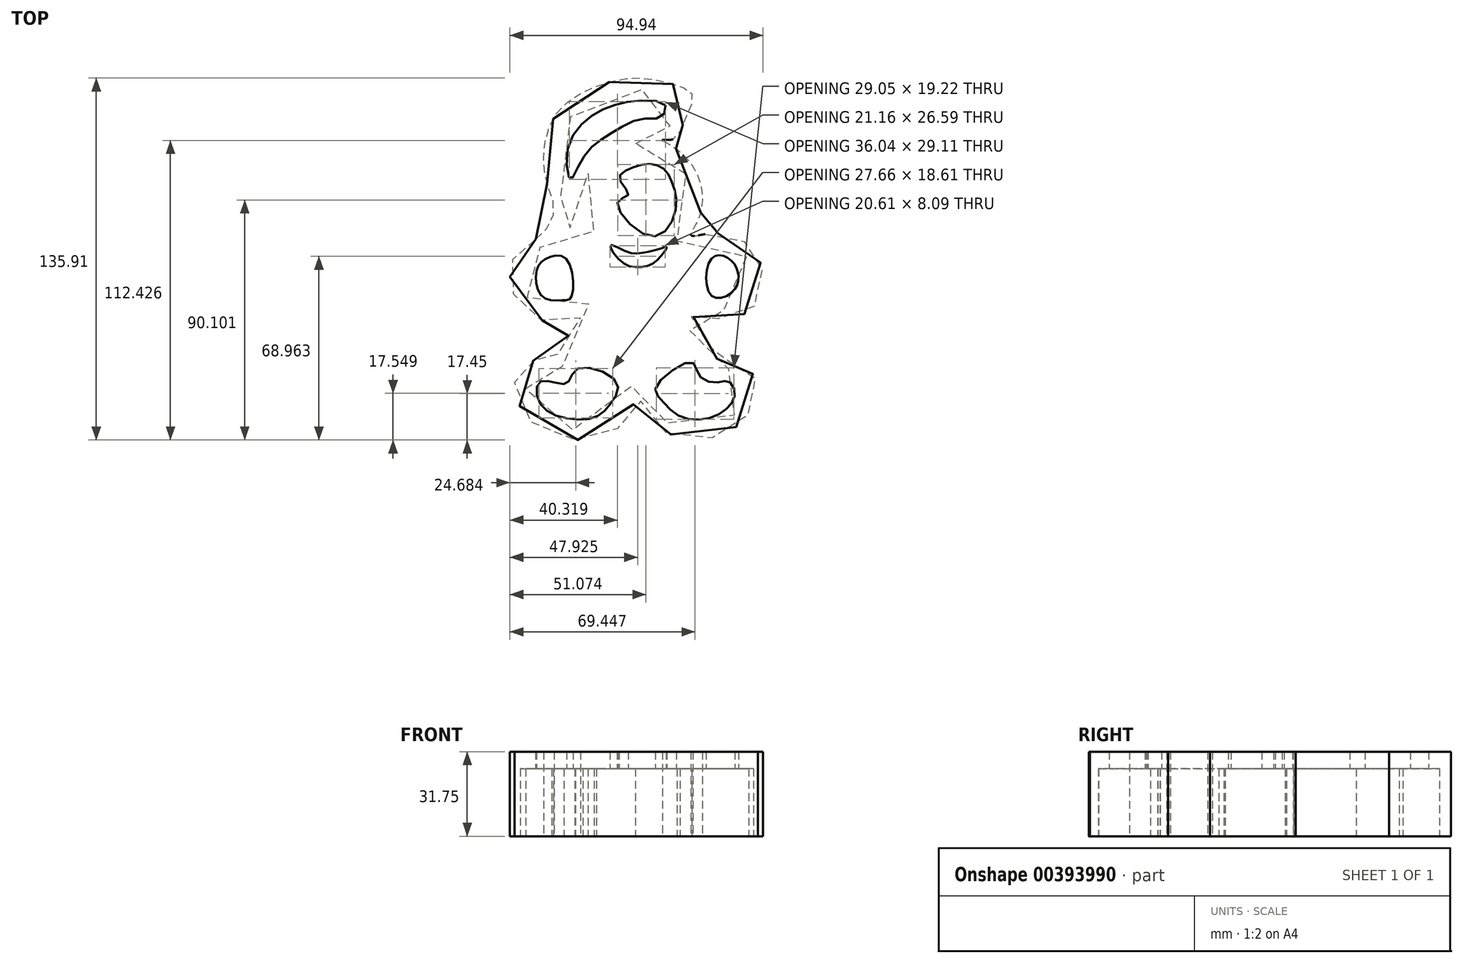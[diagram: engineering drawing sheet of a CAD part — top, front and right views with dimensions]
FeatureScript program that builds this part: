
annotation { "Feature Type Name" : "Feature", "Feature Type Description" : "" }
export const myFeature = defineFeature(function(context is Context, id is Id, definition is map)
    precondition{}
    {
        {
            var Q0;
            Q0=qCreatedBy(makeId("Top.planeOp"),FACE);
            var sketch = newSketch(context, id + "F0", { "sketchPlane" : qUnion([Q0])});
            skFitSpline(sketch, "E0", {"points": [v(2.77, 48.07) * mm, v(4.04, 51.23) * mm, v(6.56, 54.07) * mm, v(12.78, 54.07) * mm, v(14.32, 53.32) * mm, v(19.37, 63.42) * mm, v(15.75, 65.98) * mm, v(7.7, 68.06) * mm, v(-2.72, 67.77) * mm, v(-15.24, 63.3) * mm, v(-24.18, 54.95) * mm, v(-28.06, 42.43) * mm, v(-25.08, 26.94) * mm, v(-24.78, 19.78) * mm, v(-28.65, 13.82) * mm, v(-21.8, 16.5) * mm, v(-20.01, 26.64) * mm, v(-18.82, 33.5) * mm, v(-15.24, 37.07) * mm, v(-16.43, 31.1) * mm, v(-16.73, 23.36) * mm, v(-14.35, 16.8) * mm, v(-11.96, 12.73) * mm, v(-19.66, 10.97) * mm, v(-31.35, 9.54) * mm, v(-36.26, 7.28) * mm, v(-40.24, 0.64) * mm, v(-39.44, -7.19) * mm, v(-36.4, -11.3) * mm, v(-30.95, -14.22) * mm, v(-19.4, -13.3) * mm, v(-13.03, -12.37) * mm, v(-16.21, -20.6) * mm, v(-24.5, -35.1) * mm, v(-26.59, -37.48) * mm, v(-29.57, -36.58) * mm, v(-35.53, -38.07) * mm, v(-38.51, -43.74) * mm, v(-36.42, -50) * mm, v(-30.46, -55.95) * mm, v(-19.74, -59.53) * mm, v(-7.81, -56.85) * mm, v(-0.07, -45.82) * mm, v(2.92, -40.16) * mm, v(6.2, -46.12) * mm, v(12.78, -55.36) * mm, v(21.1, -59.23) * mm, v(32.12, -58.34) * mm, v(40.77, -52.97) * mm, v(44.94, -46.72) * mm, v(43.75, -40.16) * mm, v(37.79, -36.58) * mm, v(32.72, -37.18) * mm, v(28.25, -30.92) * mm, v(24.08, -23.77) * mm, v(19.6, -13.34) * mm, v(26.76, -13.34) * mm, v(36.9, -14.23) * mm, v(45.53, -8.57) * mm, v(46.43, 0.97) * mm, v(42.26, 7.82) * mm, v(30.04, 10.97) * mm, v(18.41, 10.97) * mm, v(20.5, 15.27) * mm, v(23.78, 24.81) * mm, v(21.4, 37.03) * mm, v(16.03, 43.59) * mm, v(10.07, 46.87) * mm, v(2.77, 48.07) * mm]});
            skSolve(sketch);
        }
        {
            var Q0;
            Q0=qCreatedBy(makeId("Top.planeOp"),FACE);
            var sketch = newSketch(context, id + "F1", { "sketchPlane" : qUnion([Q0])});
            skFitSpline(sketch, "E1", {"points": [v(-34.62, 12.22) * mm, v(-27.93, 22.11) * mm, v(-30.26, 32.3) * mm, v(-31.71, 45.1) * mm, v(-27.93, 57.9) * mm, v(-18.33, 66.63) * mm, v(-4.36, 71.86) * mm, v(7.28, 72.45) * mm, v(19.5, 69.54) * mm, v(24.15, 66.05) * mm, v(20.95, 56.44) * mm, v(16.88, 49.75) * mm, v(12.8, 49.46) * mm, v(17.75, 46.26) * mm, v(26.77, 34.04) * mm, v(26.19, 19.5) * mm, v(23.57, 13.68) * mm, v(30.26, 14.26) * mm, v(41.31, 12.51) * mm, v(47.42, 7.56) * mm, v(50.33, 0) * mm, v(48.88, -10.47) * mm, v(41.9, -16.58) * mm, v(31.42, -17.75) * mm, v(25.9, -17.46) * mm, v(23.57, -16.87) * mm, v(26.77, -21.82) * mm, v(33.17, -32.59) * mm, v(34.91, -34.04) * mm, v(38.99, -33.46) * mm, v(45.39, -36.66) * mm, v(48.59, -45.1) * mm, v(43.64, -55.28) * mm, v(33.46, -61.97) * mm, v(18.9, -61.97) * mm, v(8.15, -55.57) * mm, v(3.78, -48) * mm, v(-2.91, -57.6) * mm, v(-14.84, -63.13) * mm, v(-30.55, -60.51) * mm, v(-40.44, -51.2) * mm, v(-42.48, -39.86) * mm, v(-38.99, -35.2) * mm, v(-32, -32.58) * mm, v(-28.19, -33.2) * mm, v(-24.05, -26.38) * mm, v(-18.04, -17.16) * mm, v(-28.8, -18.62) * mm, v(-39.28, -14.25) * mm, v(-43.93, -5.82) * mm, v(-43.93, 2.62) * mm, v(-40.73, 8.73) * mm, v(-34.62, 12.22) * mm]});
            skSolve(sketch);
        }
        {
            var Q0;
            Q0 = qSketchRegion(id + "F1", true);
            extrude(context, id + "F2", {"entities" : qUnion([Q0]), "depth" : 31.75 * mm});
        }
        {
            var Q0;
            Q0 = qSketchRegion(id + "F0", true);
            extrude(context, id + "F3", {"entities" : qUnion([Q0]), "operationType" : NewBodyOperationType.REMOVE, "depth" : 25.4 * mm});
        }
        {
            var Q0;
            Q0=makeQuery(id+"F0.imprint","IMPRINT",FACE,{"disambiguationData":[TD([[makeQuery(id+"F0.imprint","IMPRINT",EDGE,{"derivedFrom":sQuery(id+"F0.wireOp",EDGE,"E0")}),1.0]])]});
            var sketch = newSketch(context, id + "F4", { "sketchPlane" : qUnion([Q0])});
            skFitSpline(sketch, "E2", {"points": [v(13.23, 38.72) * mm, v(7.13, 40.42) * mm, v(0, 38.39) * mm, v(-3.37, 35) * mm, v(0, 28.9) * mm, v(-4.05, 26.19) * mm, v(8.49, 13.3) * mm, v(17.64, 22.46) * mm, v(16.62, 32.96) * mm, v(13.23, 38.72) * mm]});
            skSolve(sketch);
        }
        {
            var Q0;
            Q0 = qSketchRegion(id + "F4", true);
            extrude(context, id + "F5", {"entities" : qUnion([Q0]), "operationType" : NewBodyOperationType.REMOVE, "depth" : 54.86 * mm});
        }
        {
            var Q0;
            Q0=makeQuery(id+"F0.imprint","IMPRINT",FACE,{"disambiguationData":[TD([[makeQuery(id+"F0.imprint","IMPRINT",EDGE,{"derivedFrom":sQuery(id+"F0.wireOp",EDGE,"E0")}),1.0]])]});
            var sketch = newSketch(context, id + "F6", { "sketchPlane" : qUnion([Q0])});
            skFitSpline(sketch, "E3", {"points": [v(31.2, 4.83) * mm, v(31.2, -9.06) * mm, v(39.67, -7.03) * mm, v(41.02, 0) * mm, v(37.3, 5.17) * mm, v(31.2, 4.83) * mm]});
            skFitSpline(sketch, "E4", {"points": [v(-23.37, 4.83) * mm, v(-30.83, 4.83) * mm, v(-34.55, 0) * mm, v(-32.18, -9.4) * mm, v(-24.39, -10.76) * mm, v(-21.34, -9.4) * mm, v(-23.37, 4.83) * mm]});
            skFitSpline(sketch, "E5", {"points": [v(33.57, -41.6) * mm, v(37.63, -41.26) * mm, v(40, -45.66) * mm, v(37.63, -50.75) * mm, v(30.85, -54.81) * mm, v(19.67, -54.47) * mm, v(12.55, -48.37) * mm, v(10.47, -43.06) * mm, v(23.86, -34.04) * mm, v(26.45, -38.88) * mm, v(33.57, -41.6) * mm]});
            skFitSpline(sketch, "E6", {"points": [v(-18.91, -36.37) * mm, v(-22.7, -41.6) * mm, v(-27.78, -41.6) * mm, v(-33.54, -41.6) * mm, v(-33.54, -48.71) * mm, v(-25.74, -54.47) * mm, v(-12.86, -54.81) * mm, v(-6.76, -49.73) * mm, v(-4.36, -41.6) * mm, v(-18.91, -36.37) * mm]});
            skFitSpline(sketch, "E7", {"points": [v(13.9, 62.45) * mm, v(12.21, 58.04) * mm, v(4.76, 57.36) * mm, v(-4.73, 52.96) * mm, v(-12.86, 47.54) * mm, v(-18.63, 39.74) * mm, v(-21.68, 34.66) * mm, v(-23.03, 44.15) * mm, v(-16.93, 56) * mm, v(-7.44, 61.77) * mm, v(3.4, 64.14) * mm, v(13.9, 62.45) * mm]});
            skSolve(sketch);
        }
        {
            var Q0;
            Q0 = qSketchRegion(id + "F6", true);
            extrude(context, id + "F7", {"entities" : qUnion([Q0]), "operationType" : NewBodyOperationType.REMOVE, "depth" : 75.44 * mm});
        }
        {
            var Q0;
            Q0=makeQuery(id+"F0.imprint","IMPRINT",FACE,{"disambiguationData":[TD([[makeQuery(id+"F0.imprint","IMPRINT",EDGE,{"derivedFrom":sQuery(id+"F0.wireOp",EDGE,"E0")}),1.0]])]});
            var sketch = newSketch(context, id + "F8", { "sketchPlane" : qUnion([Q0])});
            skFitSpline(sketch, "E8", {"points": [v(12.27, 8.73) * mm, v(5.3, 7.04) * mm, v(0, 7.28) * mm, v(-6.73, 9.93) * mm, v(-2.88, 3.92) * mm, v(2.99, 1.7) * mm, v(8.75, 2.76) * mm, v(12.97, 6.7) * mm, v(14.41, 9.3) * mm, v(12.27, 8.73) * mm]});
            skSolve(sketch);
        }
        {
            var Q0;
            Q0 = qSketchRegion(id + "F8", true);
            extrude(context, id + "F9", {"entities" : qUnion([Q0]), "operationType" : NewBodyOperationType.REMOVE, "depth" : 68.58 * mm});
        }
    });
